# Revit family: Porta OW
name_source: partatom
category: Doors
units: mm (PartAtom-declared; Revit-internal decimal feet)

## family parameters
Cut with Voids When Loaded = Yes
Host = Face
Room Calculation Point = No
Shared = No

## types (2) — shared parameters
Define Thermal Properties by = Schematic Type
Visor = Yes
zero-valued in all types: Default Elevation

## per-type parameters (varying)
| type | Altura Vao Luz | Altura do Visor | Espessura Folha | Largura Vao Luz | Largura do Visor | Offset | Offset Dobradica |
| 32 - 800 x 2100 | 2100 mm | 800 mm  [stored 2.62467 ft] | 32 mm  [stored 0.104987 ft] | 800 mm  [stored 2.62467 ft] | 150 mm | 45 mm  [stored 0.147638 ft] | 19 mm  [stored 0.062336 ft] |
| 40 - 1000 x 2300 | 2300 mm | 810 mm | 40 mm  [stored 0.131234 ft] | 1000 mm  [stored 3.28084 ft] | 255 mm  [stored 0.836614 ft] | 18 mm | 10 mm  [stored 0.0328084 ft] |

note: [stored X ft] marks values corroborated as IEEE doubles in the binary element streams (Revit-internal decimal feet)

## geometry (parser evidence)
native form markers: Blend x2
no freeform markers — native parametric forms only
